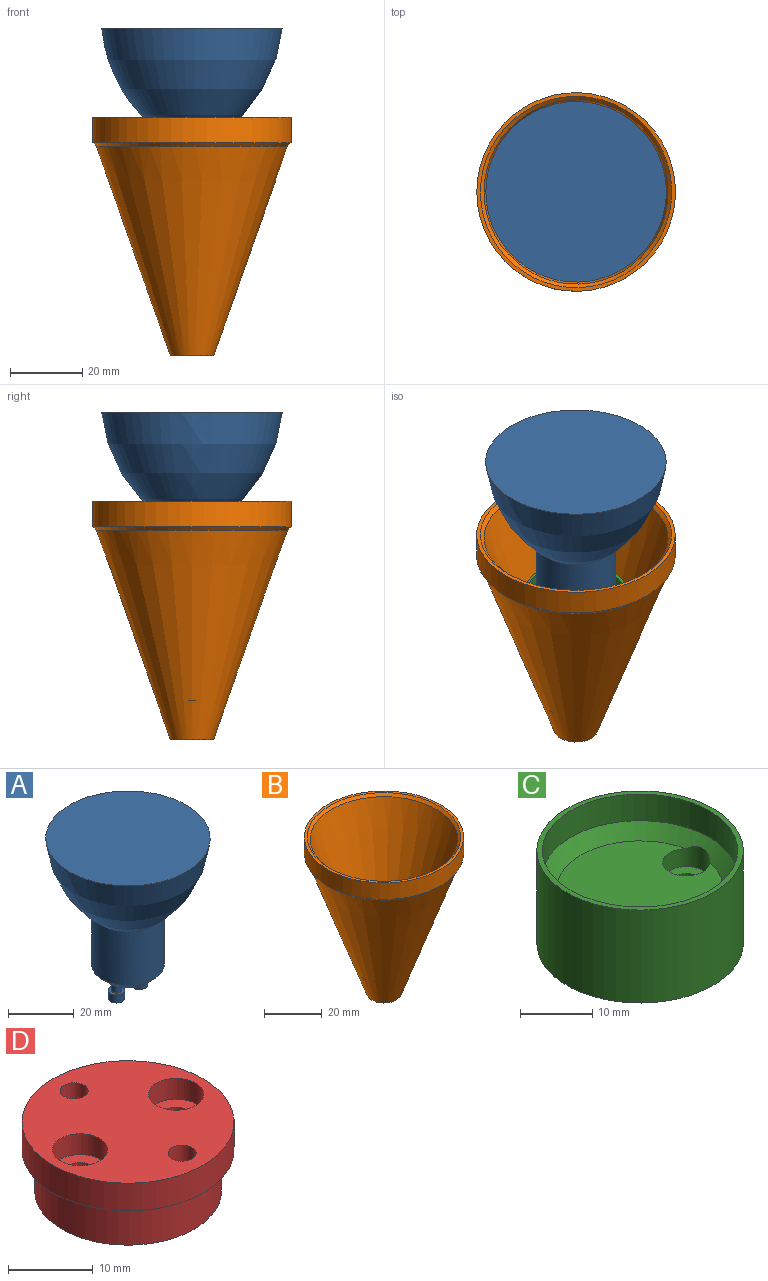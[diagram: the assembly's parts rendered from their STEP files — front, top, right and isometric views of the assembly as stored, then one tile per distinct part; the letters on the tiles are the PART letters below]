
ASSEMBLY  parts=4 mates=5
PART A: 13 faces, bbox 50x50x57 mm
  f0: cylinder r=11mm len=22mm, axis (0,0,-1), area 1382.3mm2, adj f2,f11
  f1: plane 16x16mm, normal (0,0,-1), area 186.9mm2, adj f2,f3,f4
  f2: cone r=11mm half-angle=45deg, axis (0,0,1), area 253.2mm2, adj f0,f1
  f3: cylinder r=1.5mm len=4mm, axis (0,0,1), area 37.7mm2, adj f1,f7
  f4: cylinder r=1.5mm len=4mm, axis (0,0,1), area 37.7mm2, adj f1,f10
  f5: cylinder r=2.5mm len=5mm, axis (0,0,1), area 47.1mm2, adj f6,f7
  f6: plane 5x5mm, normal (0,0,-1), area 19.6mm2, adj f5
  f7: plane 5x5mm, normal (0,0,1), area 12.6mm2, adj f3,f5
  f8: cylinder r=2.5mm len=5mm, axis (0,0,1), area 47.1mm2, adj f9,f10
  f9: plane 5x5mm, normal (0,0,-1), area 19.6mm2, adj f8
  f10: plane 5x5mm, normal (0,0,1), area 12.6mm2, adj f4,f8
  f11: revolved ~50x50mm, area 3874.9mm2, adj f0,f12
  f12: plane 50x50mm, normal (0,0,1), area 1963.5mm2, adj f11
PART B: 13 faces, bbox 55x55x66 mm
  f0: cylinder r=27.5mm len=55mm, axis (0,0,-1), area 1209.5mm2, adj f1,f8
  f1: plane 55x55mm, normal (0,0,1), area 169.6mm2, adj f0,f2
  f2: cone r=26.5mm half-angle=45deg, axis (0,0,1), area 231mm2, adj f1,f3
  f3: cone r=11mm half-angle=18.2deg, axis (0,0,1), area 5312.3mm2, adj f2,f4
  f4: plane 22x22mm, normal (0,0,1), area 284.5mm2, adj f3,f5,f9,f11
  f5: cylinder r=5mm len=21mm, axis (0,0,-1), area 659.7mm2, adj f4,f6
  f6: plane 12x12mm, normal (0,0,-1), area 34.6mm2, adj f5,f7
  f7: cone r=26.5mm half-angle=19.5deg, axis (0,0,1), area 6280.9mm2, adj f6,f8
  f8: cone r=26.5mm half-angle=45deg, axis (0,0,1), area 239.9mm2, adj f0,f7
  f9: cylinder r=1.65mm len=10mm, axis (0,0,1), area 103.7mm2, adj f4,f10
  f10: cone r=0mm half-angle=59deg, axis (0,0,1), area 10mm2, adj f9
  f11: cylinder r=1.65mm len=10mm, axis (0,0,1), area 103.7mm2, adj f4,f12
  f12: cone r=0mm half-angle=59deg, axis (0,0,1), area 10mm2, adj f11
PART C: 12 faces, bbox 28.5x28.5x15.7 mm
  f0: plane 23x22.52mm, normal (0,0,1), area 354mm2, adj f5,f8,f11
  f1: plane 28.5x28.5mm, normal (0,0,-1), area 621.9mm2, adj f2,f6,f9
  f2: cylinder r=14.25mm len=28.5mm, axis (0,0,1), area 1405.7mm2, adj f1,f3
  f3: plane 28.5x28.5mm, normal (0,0,1), area 65.4mm2, adj f2,f4
  f4: cylinder r=13.5mm len=27mm, axis (0,0,1), area 381.7mm2, adj f3,f5
  f5: cone r=13.5mm half-angle=45deg, axis (0,0,1), area 215.2mm2, adj f0,f4,f8,f11
  f6: cylinder r=1.6mm len=6.2mm, axis (0,0,1), area 62.3mm2, adj f1,f7
  f7: plane 6.5x6.5mm, normal (0,0,1), area 25.1mm2, adj f6,f8
  f8: cylinder r=3.25mm len=6.5mm, axis (0,0,1), area 63.9mm2, adj f0,f5,f7
  f9: cylinder r=1.6mm len=6.2mm, axis (0,0,1), area 62.3mm2, adj f1,f10
  f10: plane 6.5x6.5mm, normal (0,0,1), area 25.1mm2, adj f9,f11
  f11: cylinder r=3.25mm len=6.5mm, axis (0,0,1), area 63.9mm2, adj f0,f5,f10
PART D: 13 faces, bbox 25x25x10 mm
  f0: cylinder r=12.5mm len=25mm, axis (0,0,1), area 314.2mm2, adj f1,f4
  f1: plane 25x25mm, normal (0,0,1), area 407.4mm2, adj f0,f5,f6,f9,f12
  f2: plane 22x22mm, normal (0,0,-1), area 345.9mm2, adj f3,f5,f6,f7,f10
  f3: cylinder r=11mm len=22mm, axis (0,0,1), area 414.7mm2, adj f2,f4
  f4: plane 25x25mm, normal (0,0,-1), area 110.7mm2, adj f0,f3
  f5: cylinder r=1.65mm len=10mm, axis (0,0,1), area 103.7mm2, adj f1,f2
  f6: cylinder r=1.65mm len=10mm, axis (0,0,1), area 103.7mm2, adj f1,f2
  f7: cylinder r=1.65mm len=7mm, axis (0,0,1), area 72.6mm2, adj f2,f8
  f8: plane 6.5x6.5mm, normal (0,0,1), area 24.6mm2, adj f7,f9
  f9: cylinder r=3.25mm len=6.5mm, axis (0,0,1), area 61.3mm2, adj f1,f8
  f10: cylinder r=1.65mm len=7mm, axis (0,0,1), area 72.6mm2, adj f2,f11
  f11: plane 6.5x6.5mm, normal (0,0,1), area 24.6mm2, adj f10,f12
  f12: cylinder r=3.25mm len=6.5mm, axis (0,0,1), area 61.3mm2, adj f1,f11
PLACE A t=(0,0,40.71)mm
PLACE B at identity fixed
PLACE C rot(axis=(0,0,1),90deg) t=(-0.18,0,31)mm
PLACE D t=(-0.18,0,21)mm
MATE revolute C.f9 <-> D.f5  axis (0,0,-1) through (-0.18,9,31)mm
MATE revolute D.f10 <-> B.f11  axis (0,0,-1) through (7.82,0,21)mm
MATE revolute C.f6 <-> D.f6  axis (0,0,-1) through (-0.18,-9,31)mm
MATE revolute D.f7 <-> B.f9  axis (0,0,-1) through (-8.18,0,21)mm
MATE cylindrical B.f0 <-> A.f0  axis (0,0,1) through (0,0,58)mm
